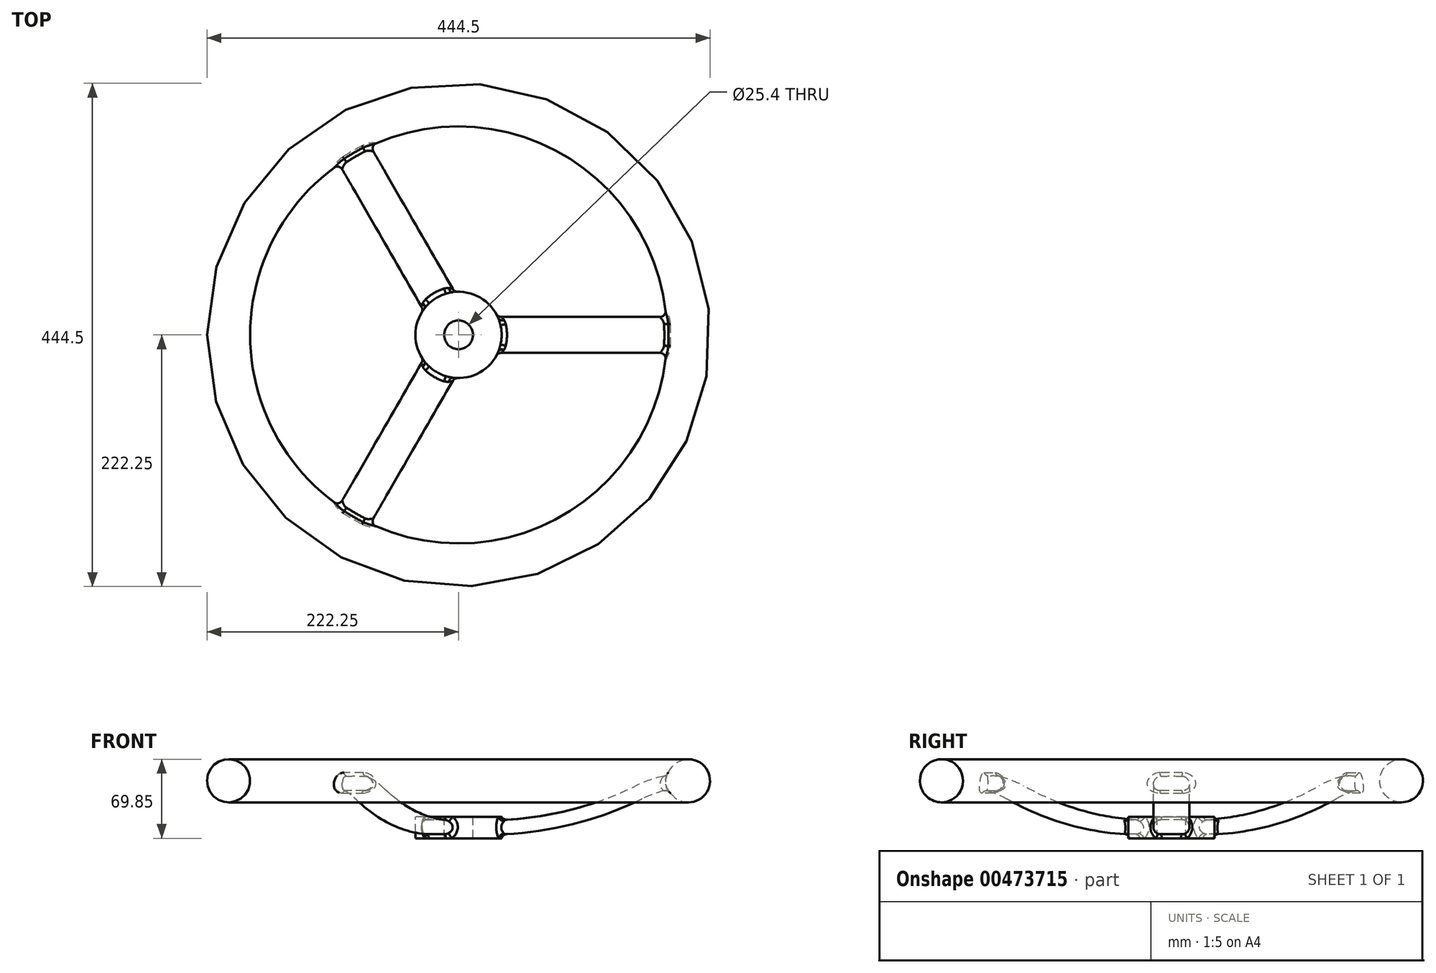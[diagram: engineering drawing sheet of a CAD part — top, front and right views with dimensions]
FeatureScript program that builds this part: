
annotation { "Feature Type Name" : "Feature", "Feature Type Description" : "" }
export const myFeature = defineFeature(function(context is Context, id is Id, definition is map)
    precondition{}
    {
        {
            var Q0;
            Q0=qCreatedBy(makeId("Front.planeOp"),FACE);
            var sketch = newSketch(context, id + "F0", { "sketchPlane" : qUnion([Q0])});
            skLineSegment(sketch, "E0.bottom", {"start": v(0, 0) * mm, "end": v(203.2, 0) * mm, "construction": true});
            skLineSegment(sketch, "E0.top", {"start": v(0, -50.8) * mm, "end": v(203.2, -50.8) * mm, "construction": true});
            skLineSegment(sketch, "E0.left", {"start": v(0, 0) * mm, "end": v(0, -50.8) * mm, "construction": true});
            skLineSegment(sketch, "E0.right", {"start": v(203.2, 0) * mm, "end": v(203.2, -50.8) * mm, "construction": true});
            skCircle(sketch, "E1", {"center": v(203.2, 0) * mm, "radius": 19.05 * mm});
            skLineSegment(sketch, "E2.bottom", {"start": v(38.1, -50.8) * mm, "end": v(12.7, -50.8) * mm});
            skLineSegment(sketch, "E2.top", {"start": v(38.1, -31.75) * mm, "end": v(12.7, -31.75) * mm});
            skLineSegment(sketch, "E2.left", {"start": v(38.1, -50.8) * mm, "end": v(38.1, -31.75) * mm});
            skLineSegment(sketch, "E2.right", {"start": v(12.7, -50.8) * mm, "end": v(12.7, -31.75) * mm});
            skPoint(sketch, "E2.middle", {"position": v(25.4, -41.27) * mm});
            skLineSegment(sketch, "E3", {"start": v(25.4, -41.27) * mm, "end": v(106.38, -41.27) * mm, "construction": true});
            skArc(sketch, "E4", {"start": v(25.4, -41.28) * mm, "mid": v(94.32, -33.38) * mm, "end": v(159.68, -10.1) * mm});
            skArc(sketch, "E5", {"start": v(203.2, 0) * mm, "mid": v(180.86, -2.56) * mm, "end": v(159.68, -10.1) * mm});
            skSolve(sketch);
        }
        {
            var Q0;
            Q0=sQuery(id+"F0.wireOp",VERTEX,"E1.center");
            var Q1;
            Q1=sQuery(id+"F0.wireOp",EDGE,"E0.bottom");
            cPlane(context, id + "F1", {"entities" : qUnion([Q0, Q1]), "cplaneType" : CPlaneType.LINE_POINT, "offset" : 25.4 * mm, "width" : 152.4 * mm, "height" : 152.4 * mm});
        }
        {
            var Q0;
            Q0=qCreatedBy(id+"F1.planeOp",FACE);
            var sketch = newSketch(context, id + "F2", { "sketchPlane" : qUnion([Q0])});
            skLineSegment(sketch, "E6.bottom", {"start": v(-9.53, -6.35) * mm, "end": v(9.52, -6.35) * mm});
            skLineSegment(sketch, "E6.top", {"start": v(-9.52, 6.35) * mm, "end": v(9.53, 6.35) * mm});
            skLineSegment(sketch, "E6.left", {"start": v(-15.88, 0) * mm, "end": v(-15.88, 0) * mm});
            skLineSegment(sketch, "E6.right", {"start": v(15.88, 0) * mm, "end": v(15.88, 0) * mm});
            skPoint(sketch, "E6.middle", {"position": v(0, 0) * mm});
            skPoint(sketch, "E7.visualSharp", {"position": v(-15.88, -6.35) * mm});
            skArc(sketch, "E7.filletArc", {"start": v(-15.88, 0) * mm, "mid": v(-14.02, -4.5) * mm, "end": v(-9.53, -6.35) * mm});
            skPoint(sketch, "E8.visualSharp", {"position": v(-15.88, 6.35) * mm});
            skArc(sketch, "E8.filletArc", {"start": v(-9.53, 6.35) * mm, "mid": v(-14.02, 4.5) * mm, "end": v(-15.87, 0) * mm});
            skPoint(sketch, "E9.visualSharp", {"position": v(15.87, 6.35) * mm});
            skArc(sketch, "E9.filletArc", {"start": v(15.87, 0) * mm, "mid": v(14.02, 4.5) * mm, "end": v(9.53, 6.35) * mm});
            skPoint(sketch, "E10.visualSharp", {"position": v(15.88, -6.35) * mm});
            skArc(sketch, "E10.filletArc", {"start": v(9.52, -6.35) * mm, "mid": v(14.02, -4.5) * mm, "end": v(15.87, 0) * mm});
            skSolve(sketch);
        }
        {
            var Q0;
            {var subQ3=sQuery(id+"F0.wireOp",EDGE,"E2.bottom");Q0=makeQuery(id+"F0.imprint","IMPRINT",FACE,{"disambiguationData":[TD([[makeQuery(id+"F0.imprint","IMPRINT",EDGE,{"derivedFrom":subQ3}),-1.0]])]});}
            var Q1;
            Q1=makeQuery(id+"F0.imprint","IMPRINT",FACE,{"disambiguationData":[TD([[makeQuery(id+"F0.imprint","IMPRINT",EDGE,{"derivedFrom":sQuery(id+"F0.wireOp",EDGE,"E1")}),1.0]])]});
            var Q2;
            Q2=sQuery(id+"F0.wireOp",EDGE,"E0.left");
            revolve(context, id + "F3", {"entities" : qUnion([Q0, Q1]), "axis" : qUnion([Q2]), "revolveType" : RevolveType.FULL});
        }
        {
            var Q0;
            Q0=makeQuery(id+"F2.imprint","IMPRINT",FACE,{"disambiguationData":[TD([[makeQuery(id+"F2.imprint","IMPRINT",EDGE,{"derivedFrom":sQuery(id+"F2.wireOp",EDGE,"E6.bottom")}),1.0]])]});
            var Q1;
            Q1=sQuery(id+"F0.wireOp",EDGE,"E5");
            var Q2;
            Q2=sQuery(id+"F0.wireOp",EDGE,"E4");
            sweep(context, id + "F4", {"profiles" : qUnion([Q0]), "path" : qUnion([Q1, Q2])});
        }
        {
            var Q0;
            Q0=makeQuery(id+"F4.opSweep","SWEPT_BODY",BODY,{"disambiguationData":[OSD([sQuery(id+"F0.wireOp",EDGE,"E4"),sQuery(id+"F2.wireOp",EDGE,"E6.bottom"),sQuery(id+"F2.wireOp",EDGE,"E6.top"),sQuery(id+"F2.wireOp",EDGE,"E7.filletArc"),sQuery(id+"F2.wireOp",EDGE,"E8.filletArc"),sQuery(id+"F2.wireOp",EDGE,"E9.filletArc"),sQuery(id+"F2.wireOp",EDGE,"E10.filletArc")])]});
            var Q1;
            Q1=makeQuery(id+"F3.opRevolve","SWEPT_FACE",FACE,{"disambiguationData":[OSD([sQuery(id+"F0.wireOp",EDGE,"E1")])]});
            circularPattern(context, id + "F5", {"entities" : qUnion([Q0]), "axis" : qUnion([Q1]), "angle" : 360 * degree, "instanceCount" : 3, "equalSpace" : true});
        }
        {
            var Q0;
            Q0=makeQuery(id+"F3.opRevolve","SWEPT_BODY",BODY,{"disambiguationData":[OSD([sQuery(id+"F0.wireOp",EDGE,"E2.bottom"),sQuery(id+"F0.wireOp",EDGE,"E2.top"),sQuery(id+"F0.wireOp",EDGE,"E2.left"),sQuery(id+"F0.wireOp",EDGE,"E2.right")])]});
            var Q1;
            Q1=makeQuery(id+"F5.opPattern","COPY",BODY,{"derivedFrom":makeQuery(id+"F4.opSweep","SWEPT_BODY",BODY,{"disambiguationData":[OSD([sQuery(id+"F0.wireOp",EDGE,"E4"),sQuery(id+"F2.wireOp",EDGE,"E6.bottom"),sQuery(id+"F2.wireOp",EDGE,"E6.top"),sQuery(id+"F2.wireOp",EDGE,"E7.filletArc"),sQuery(id+"F2.wireOp",EDGE,"E8.filletArc"),sQuery(id+"F2.wireOp",EDGE,"E9.filletArc"),sQuery(id+"F2.wireOp",EDGE,"E10.filletArc")])]}),"instanceName":"2"});
            var Q2;
            Q2=makeQuery(id+"F4.opSweep","SWEPT_BODY",BODY,{"disambiguationData":[OSD([sQuery(id+"F0.wireOp",EDGE,"E4"),sQuery(id+"F2.wireOp",EDGE,"E6.bottom"),sQuery(id+"F2.wireOp",EDGE,"E6.top"),sQuery(id+"F2.wireOp",EDGE,"E7.filletArc"),sQuery(id+"F2.wireOp",EDGE,"E8.filletArc"),sQuery(id+"F2.wireOp",EDGE,"E9.filletArc"),sQuery(id+"F2.wireOp",EDGE,"E10.filletArc")])]});
            var Q3;
            Q3=makeQuery(id+"F5.opPattern","COPY",BODY,{"derivedFrom":makeQuery(id+"F4.opSweep","SWEPT_BODY",BODY,{"disambiguationData":[OSD([sQuery(id+"F0.wireOp",EDGE,"E4"),sQuery(id+"F2.wireOp",EDGE,"E6.bottom"),sQuery(id+"F2.wireOp",EDGE,"E6.top"),sQuery(id+"F2.wireOp",EDGE,"E7.filletArc"),sQuery(id+"F2.wireOp",EDGE,"E8.filletArc"),sQuery(id+"F2.wireOp",EDGE,"E9.filletArc"),sQuery(id+"F2.wireOp",EDGE,"E10.filletArc")])]}),"instanceName":"1"});
            var Q4;
            Q4=makeQuery(id+"F3.opRevolve","SWEPT_BODY",BODY,{"disambiguationData":[OSD([sQuery(id+"F0.wireOp",EDGE,"E1")])]});
            booleanBodies(context, id + "F6", {"operationType" : BooleanOperationType.UNION, "tools" : qUnion([Q0, Q1, Q2, Q3, Q4])});
        }
        {
            var Q0;
            Q0=makeQuery(id+"F3.opRevolve","SWEPT_FACE",FACE,{"disambiguationData":[OSD([sQuery(id+"F0.wireOp",EDGE,"E1")])]});
            var Q1;
            Q1=makeQuery(id+"F5.opPattern","COPY",FACE,{"derivedFrom":makeQuery(id+"F4.opSweep","SWEPT_FACE",FACE,{"disambiguationData":[OSD([sQuery(id+"F0.wireOp",EDGE,"E4"),sQuery(id+"F2.wireOp",EDGE,"E6.top")])]}),"instanceName":"2"});
            var Q2;
            Q2=makeQuery(id+"F5.opPattern","COPY",FACE,{"derivedFrom":makeQuery(id+"F4.opSweep","SWEPT_FACE",FACE,{"disambiguationData":[OSD([sQuery(id+"F0.wireOp",EDGE,"E4"),sQuery(id+"F2.wireOp",EDGE,"E6.top")])]}),"instanceName":"1"});
            var Q3;
            Q3=makeQuery(id+"F6.opBoolean","INTERSECT",EDGE,{"derivedFrom":[makeQuery(id+"F3.opRevolve","SWEPT_FACE",FACE,{"disambiguationData":[OSD([sQuery(id+"F0.wireOp",EDGE,"E2.left")])]}),makeQuery(id+"F4.opSweep","SWEPT_FACE",FACE,{"disambiguationData":[OSD([sQuery(id+"F0.wireOp",EDGE,"E4"),sQuery(id+"F2.wireOp",EDGE,"E6.top")])]})]});
            fillet(context, id + "F7", {"entities" : qUnion([Q0, Q1, Q2, Q3]), "radius" : 5.08 * mm, "tangentPropagation" : true, "allowEdgeOverflow" : false});
        }
    });
